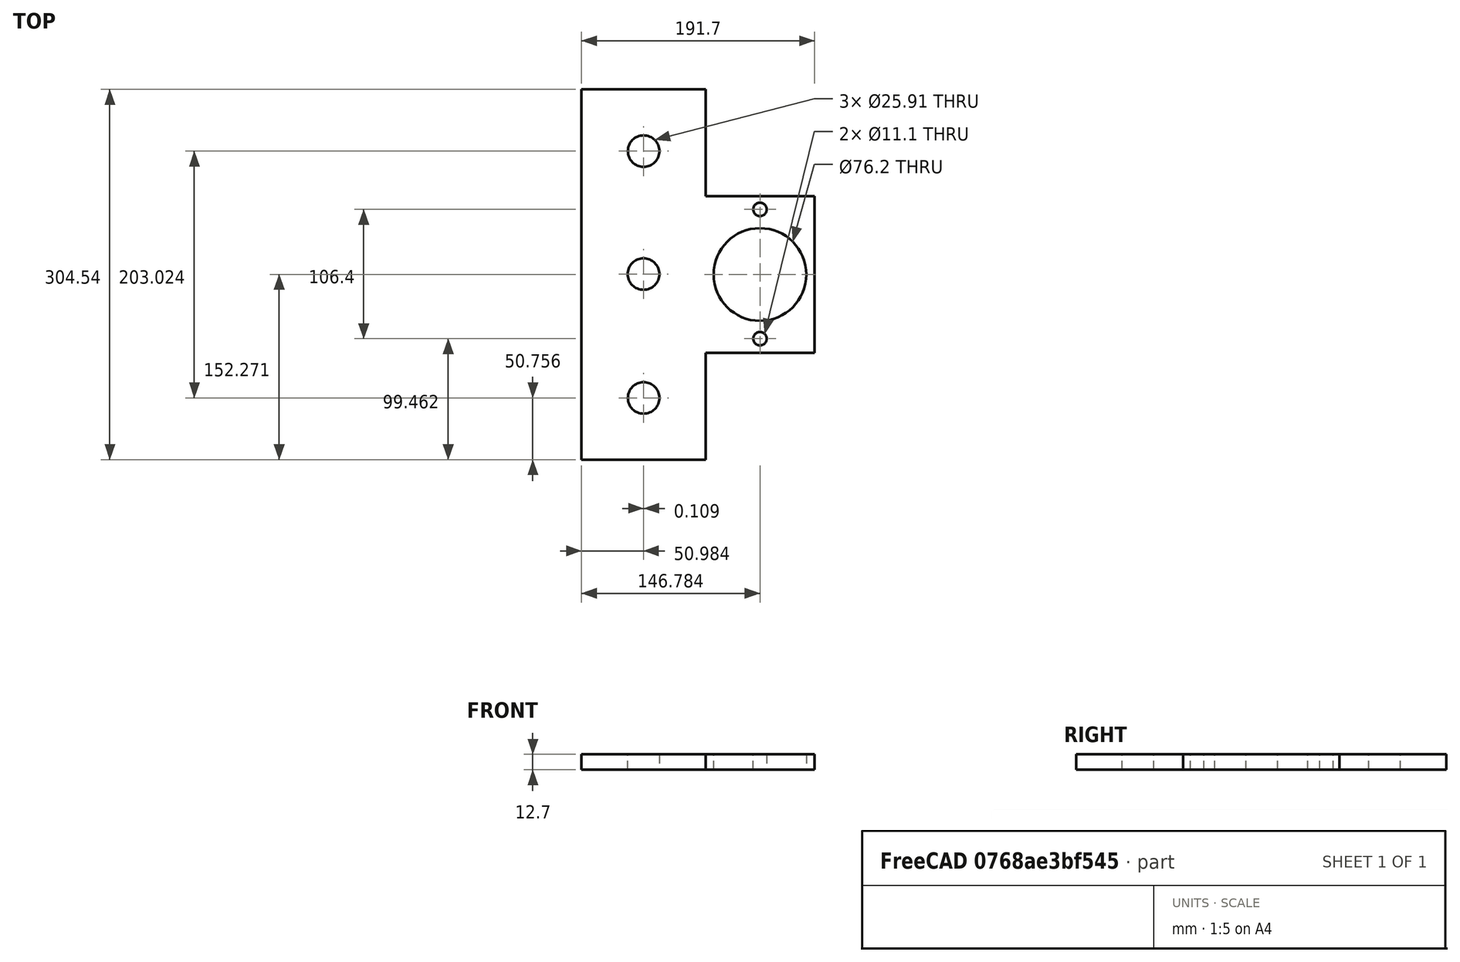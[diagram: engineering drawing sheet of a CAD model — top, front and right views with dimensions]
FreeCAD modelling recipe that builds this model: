
FCSTD DOCUMENT  (FreeCAD 0.16R6712 (Git))
Label: PTO Motor Mount plate
License: All rights reserved
LicenseURL: http://en.wikipedia.org/wiki/All_rights_reserved
objects: Sketcher::SketchObject×1, PartDesign::Pad×1
note: 3 computed .brp shape members not serialized (recipe doc carries the construction recipe); baked Part::Feature solids carry a one-line shape summary decoded from their .brp

FEATURE [Sketcher::SketchObject] Sketch006
  Placement = pos=(0,0,-101.6) rot=(1,0,0;3.14159rad)
  sketch-geometry (18):
    g0: Circle CenterX=-79.856 CenterY=-35.9206 CenterZ=0 NormalX=0 NormalY=0 NormalZ=1 Radius=38.1
    g1: Circle CenterX=-79.856 CenterY=16.888 CenterZ=0 NormalX=0 NormalY=0 NormalZ=1 Radius=5.55
    g2: Circle CenterX=-79.856 CenterY=-89.512 CenterZ=0 NormalX=0 NormalY=0 NormalZ=1 Radius=5.55
    g3: LineSegment StartX=-226.64 StartY=116.351 StartZ=0 EndX=-226.64 EndY=-188.192 EndZ=0
    g4: LineSegment StartX=-226.64 StartY=-188.192 StartZ=0 EndX=-124.453 EndY=-188.192 EndZ=0
    g5: LineSegment StartX=-124.453 StartY=-100.279 StartZ=0 EndX=-124.453 EndY=-188.192 EndZ=0
    g6: LineSegment StartX=-124.453 StartY=28.438 StartZ=0 EndX=-124.453 EndY=116.351 EndZ=0
    g7: LineSegment StartX=-124.453 StartY=28.438 StartZ=0 EndX=-34.9357 EndY=28.438 EndZ=0
    g8: LineSegment StartX=-124.453 StartY=-100.279 StartZ=0 EndX=-34.9357 EndY=-100.279 EndZ=0
    g9: LineSegment StartX=-34.9357 StartY=-100.279 StartZ=0 EndX=-34.9357 EndY=28.438 EndZ=0
    g10: LineSegment StartX=-226.64 StartY=116.351 StartZ=0 EndX=-124.453 EndY=116.351 EndZ=0
    g11: LineSegment [constr] StartX=-34.9357 StartY=-35.9206 StartZ=0 EndX=-226.456 EndY=-35.9206 EndZ=0
    g12: LineSegment [constr] StartX=-175.547 StartY=116.351 StartZ=0 EndX=-175.547 EndY=-188.192 EndZ=0
    g13: Circle CenterX=-175.656 CenterY=-36.312 CenterZ=0 NormalX=0 NormalY=0 NormalZ=1 Radius=12.954
    g14: LineSegment [constr] StartX=-124.453 StartY=65.5943 StartZ=0 EndX=-226.64 EndY=65.5943 EndZ=0
    g15: LineSegment [constr] StartX=-124.453 StartY=-137.43 StartZ=0 EndX=-226.64 EndY=-137.43 EndZ=0
    g16: Circle CenterX=-175.547 CenterY=65.5943 CenterZ=0 NormalX=0 NormalY=0 NormalZ=1 Radius=12.954
    g17: Circle CenterX=-175.547 CenterY=-137.43 CenterZ=0 NormalX=0 NormalY=0 NormalZ=1 Radius=12.954
  constraints (49):
    c: Coincident(g4,g3)
    c: Coincident(g5,g4)
    c: Horizontal(g7)
    c: Horizontal(g8)
    c: Coincident(g9,g8)
    c: Coincident(g9,g7)
    c: Vertical(g9)
    c: Coincident(g10,g3)
    c: Coincident(g10,g6)
    c: Equal(g8,g7)
    c: Coincident(g7,g6)
    c: Coincident(g8,g5)
    c: PointOnObject(g11,g9)
    c: PointOnObject(g0,g11)
    c: Symmetric(g7,g8,g11)
    c: DistanceY(g6) = 28.438
    c: Equal(g10,g4)
    c: Symmetric(g3,g3,g11)
    c: Symmetric(g5,g6,g11)
    c: Radius(g0) = 38.1
    c: Equal(g1,g2)
    c: Symmetric(g6,g4,g11)
    c: PointOnObject(g12,g10)
    c: PointOnObject(g12,g4)
    c: Vertical(g12)
    c: Radius(g13) = 12.954
    c: Symmetric(g3,g4,g12)
    c: Symmetric(g3,g6,g12)
    c: PointOnObject(g14,g6)
    c: PointOnObject(g14,g3)
    c: PointOnObject(g15,g5)
    c: PointOnObject(g15,g3)
    c: Horizontal(g15)
    c: Horizontal(g14)
    c: DistanceY(g3,g15) = 50.7627
    c: DistanceY(g14,g3) = 50.7568
    c: Equal(g15,g14)
    c: PointOnObject(g16,g14)
    c: PointOnObject(g16,g12)
    c: PointOnObject(g17,g15)
    c: PointOnObject(g17,g12)
    c: Equal(g17,g16)
    c: Equal(g16,g13)
    c: DistanceX(g11) = -226.456
    c: DistanceY(g11) = -35.9206
    c: DistanceX(g11) = -34.9357
    c: DistanceX(g6) = -124.453
    c: DistanceY(g6) = 116.351
    c: DistanceX(g0) = -79.856
FEATURE [PartDesign::Pad] Pad
  Length = 12.7
  Length2 = 100
  Placement = pos=(0,0,-101.6) rot=(1,0,0;3.14159rad)
  Sketch = -> Sketch006
  Type = 0
